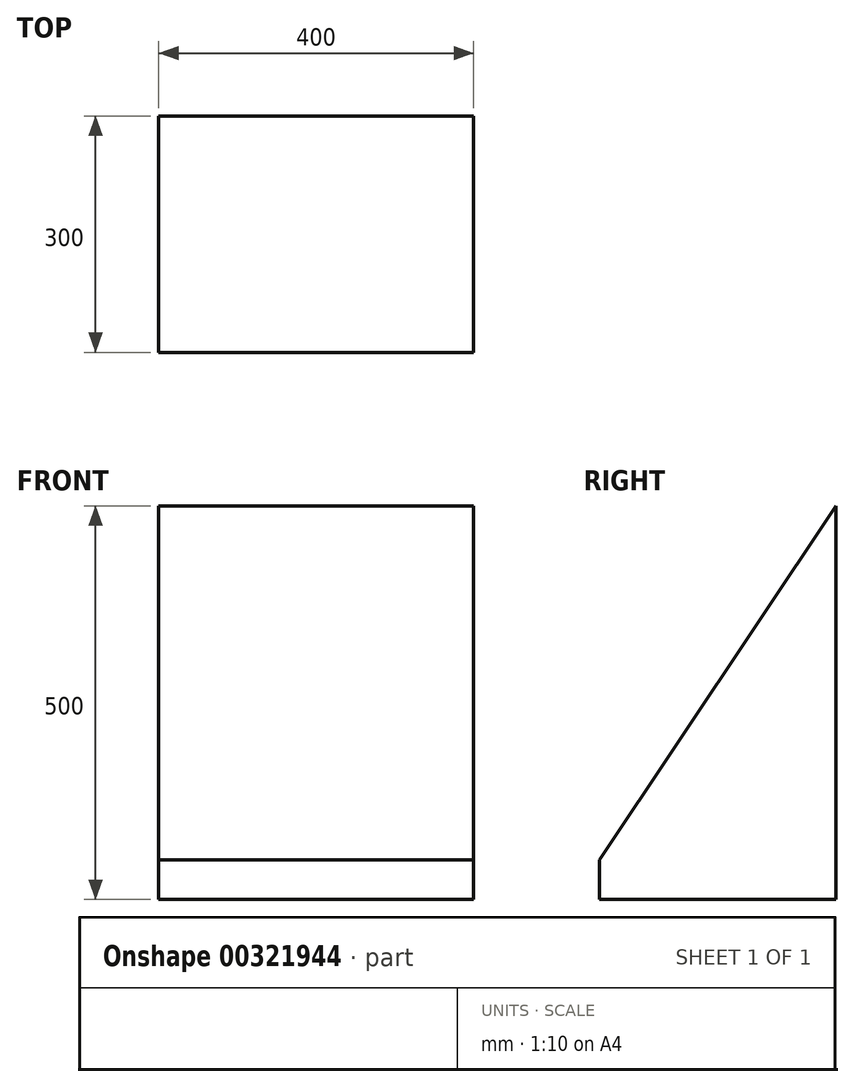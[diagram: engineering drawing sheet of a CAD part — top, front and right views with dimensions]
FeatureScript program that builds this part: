
annotation { "Feature Type Name" : "Feature", "Feature Type Description" : "" }
export const myFeature = defineFeature(function(context is Context, id is Id, definition is map)
    precondition{}
    {
        {
            var Q0;
            Q0=qCreatedBy(makeId("Right.planeOp"),FACE);
            var sketch = newSketch(context, id + "F0", { "sketchPlane" : qUnion([Q0])});
            skLineSegment(sketch, "E0.top", {"start": v(150, -250) * mm, "end": v(-150, -250) * mm});
            skLineSegment(sketch, "E0.left", {"start": v(150, 250) * mm, "end": v(150, -250) * mm});
            skLineSegment(sketch, "E0.right", {"start": v(-150, -200) * mm, "end": v(-150, -250) * mm});
            skPoint(sketch, "E0.middle", {"position": v(0, 0) * mm});
            skLineSegment(sketch, "E1", {"start": v(150, 250) * mm, "end": v(-150, -200) * mm});
            skPoint(sketch, "E2.orphan", {"position": v(-150, 250) * mm});
            skSolve(sketch);
        }
        {
            var Q0;
            Q0=makeQuery(id+"F0.imprint","IMPRINT",FACE,{"disambiguationData":[TD([[makeQuery(id+"F0.imprint","IMPRINT",EDGE,{"derivedFrom":sQuery(id+"F0.wireOp",EDGE,"E0.top")}),-1.0]])]});
            extrude(context, id + "F1", {"entities" : qUnion([Q0]), "endBound" : BoundingType.SYMMETRIC, "depth" : 400 * mm});
        }
    });
